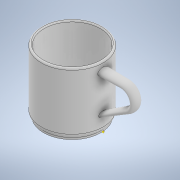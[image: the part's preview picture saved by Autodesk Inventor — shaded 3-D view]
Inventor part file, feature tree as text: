
AUTODESK INVENTOR PART (.ipt)
format: ipt  version: 2022 (Build 260153000, 153)  size: 252,928 bytes
history: native  units: mm
features: sketch x8, other x4, plane x2, revolve x1, shell x1, loft x1, fillet x1, extrude x1
ambient origin geometry x8: Origin, YZ Plane, XZ Plane, XY Plane, X Axis, Y Axis, Z Axis, Center Point
bodies: Solid1 (feature_tree)
feature tree (19):
  other  "CrossSection1"
  revolve  "Revolution1"  [1 undecoded]
  shell  "Shell1"  Thickness=65.0mm
  sketch  "Sketch2"  dims[d3=6.25mm d4=9.272934mm d5=90.0deg]
  other  "Work Point1"
  plane  "Work Plane1"
  sketch  "Sketch3"  dims[d6=3.0mm d7=0.5mm d8=2.0mm d9=0.0mm d10=20.0mm]
  other  "Work Point2"
  other  "Work Point3"
  sketch  "Sketch4"  dims[d15=25.0mm]
  plane  "Work Plane2"
  loft  "Loft1"
  fillet  "Fillet1"  [1 undecoded]
  sketch  "Sketch6"  dims[d17=12.0mm]
  sketch  "Sketch7"  dims[d18=15.0mm]
  extrude  "Extrusion1"  Depth=2.0mm TaperAngle=0.0deg
  sketch  "Sketch1"  dims[d0=70.0mm d1=35.0mm d2=65.0mm]
  sketch  "Sketch5"  dims[d16=10.0mm]
  sketch  "Sketch8"  dims[d19=4.0mm d20=6.0mm d21=3.0mm d22=5.0mm d23=0.0mm d24=90.0deg d25=0.0mm d26=90.0deg d27=0.0mm d28=90.0deg d29=2.0mm d30=65.0mm d31=62.0mm d32=2.0mm d33=0.0mm]
note: 2 required parameter values undecoded (feature->parameter linkage not recoverable at this tier; creation-order binding heuristic only, values carry confidence <= 0.55)